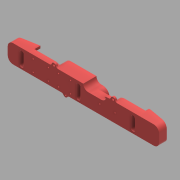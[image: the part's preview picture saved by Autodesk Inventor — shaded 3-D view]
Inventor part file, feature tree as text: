
AUTODESK INVENTOR PART (.ipt)
format: ipt  version: 2017 (Build 210142000, 142)  size: 804,864 bytes
history: native  units: mm
features: reference x26, sketch x14, extrude x13, projected_geometry x10, fillet x9, other x9, chamfer x3, hole x2
ambient origin geometry x8: Origin, YZ Plane, XZ Plane, XY Plane, X Axis, Y Axis, Z Axis, Center Point
bodies: Solid1 (feature_tree)
feature tree (86):
  extrude  "Extrusion1"  TaperAngle=0.0deg  [1 undecoded]
  extrude  "Extrusion4"  Depth=17.453293mm
  extrude  "Extrusion5"  Depth=4.6mm
  fillet  "Fillet1"  Radius=4.6mm
  hole  "Hole1"  [1 undecoded]
  extrude  "Extrusion8"  Depth=2.5mm
  extrude  "Extrusion9"  Depth=3.0mm
  extrude  "Extrusion10"  Depth=1.6mm
  fillet  "Fillet5"  Radius=1.6mm
  extrude  "Extrusion11"  Depth=2.0mm TaperAngle=0.0deg
  fillet  "Fillet6"  Radius=10.0mm
  extrude  "Extrusion12"  Depth=4.0mm
  extrude  "Extrusion13"  Depth=1.2mm
  fillet  "Fillet7"  Radius=1.2mm
  fillet  "Fillet8"  Radius=3.0mm
  fillet  "Fillet9"  Radius=3.0mm
  fillet  "Fillet10"  Radius=3.0mm
  extrude  "Extrusion14"  Depth=2.0mm
  fillet  "Fillet11"  Radius=2.0mm
  sketch  "Sketch17"  dims[d76=1.75mm d77=25.0mm d78=2.0mm]
  extrude  "Extrusion15"  Depth=3.0mm TaperAngle=0.0deg
  fillet  "Fillet12"  Radius=4.75mm
  hole  "Hole4"  [1 undecoded]
  extrude  "Extrusion16"  Depth=2.0mm
  chamfer  "Chamfer1"  Distance=16.0mm
  extrude  "Extrusion17"  Depth=2.0mm
  chamfer  "Chamfer2"  Distance=3.5mm
  chamfer  "Chamfer3"  Distance=4.6mm
  sketch  "Sketch1"  dims[d0=17.453293mm d1=0.0mm]
  reference  "Reference1"
  reference  "Reference2"
  reference  "Reference3"
  reference  "Reference4"
  reference  "Reference5"
  reference  "Reference6"
  sketch  "Sketch4"  dims[d2=0.0mm d3=17.453293mm]
  projected_geometry  "Projected Loop3"
  reference  "Reference7"
  reference  "Reference8"
  reference  "Reference9"
  reference  "Reference10"
  reference  "Reference11"
  reference  "Reference12"
  reference  "Reference13"
  sketch  "Sketch5"  dims[d4=20.0mm d5=0.0mm d6=8.0mm d16=4.6mm]
  projected_geometry  "Projected Loop4"
  projected_geometry  "Projected Loop5"
  reference  "Reference18"
  reference  "Reference19"
  reference  "Reference20"
  reference  "Reference21"
  reference  "Reference22"
  reference  "Reference23"
  reference  "Reference24"
  reference  "Reference25"
  sketch  "Sketch9"  dims[d17=1.5mm d18=0.0mm d19=4.6mm]
  sketch  "Sketch10"  dims[d20=4.6mm d21=2.5mm]
  reference  "Reference29"
  sketch  "Sketch11"  dims[d22=1.5mm d23=0.0mm d24=3.0mm]
  projected_geometry  "Projected Loop7"
  projected_geometry  "Projected Loop12"
  projected_geometry  "Projected Loop13"
  sketch  "Sketch13"  dims[d32=1.4mm d33=6.0mm d34=4.0mm d35=2.0mm d36=90.0deg d37=8.0mm d38=20.594885mm d48=1.6mm d49=1.6mm]
  projected_geometry  "Projected Loop14"
  sketch  "Sketch14"  dims[d50=2.0mm d51=0.0mm d52=2.0mm d53=0.0mm d54=10.0mm]
  projected_geometry  "Projected Loop15"
  sketch  "Sketch15"  dims[d55=4.0mm d56=0.0mm d67=16.5mm]
  projected_geometry  "Projected Loop16"
  projected_geometry  "Projected Loop17"
  sketch  "Sketch16"  dims[d69=3.5mm d70=1.2mm d71=1.2mm d72=3.0mm d73=3.0mm d74=3.0mm d75=0.0mm]
  sketch  "Sketch18"  dims[d79=3.0mm d80=0.0mm d81=3.0mm d82=0.0mm d83=4.75mm]
  sketch  "Sketch19"  dims[d84=5.75mm d85=7.25mm]
  reference  "Reference30"
  reference  "Reference31"
  sketch  "Sketch20"  dims[d86=5.0mm d87=158.0mm d88=16.0mm d89=64.0mm d90=3.5mm d91=4.6mm d92=4.6mm d93=2.0mm d94=0.0mm d95=51.5mm d96=21.5mm d97=4.6mm d98=2.5mm d99=4.6mm d100=2.0mm d101=0.0mm d102=4.6mm d103=4.6mm d104=7.0mm d105=2.2mm d106=6.0mm d107=4.0mm d108=2.0mm d109=90.0deg d110=8.0mm d111=20.594885mm d112=2.0mm d113=0.0mm d114=0.5mm d115=2.0mm d116=45.0deg d117=2.0mm d118=0.0mm d119=0.5mm d120=2.0mm d121=45.0deg d122=0.5mm d123=2.0mm d124=45.0deg]
  reference  "Reference32"
  reference  "Reference33"
  other  "<userpath>\Dropbox\Work\HeadSLAM\xtion_custom_assembly.iam"
  other  "xtion_custom_assembly.iam"
  other  "xtion_heatsink:1"
  other  "xtion_projector:1"
  other  "xtion_mainboard:1"
  other  "xtion_rgb_cam:1"
  other  "xtion_ir_cam:1"
  other  "<userpath>\Dropbox\Work\HeadSLAM\xtion_custom_assembly_v2.iam"
  other  "xtion_custom_assembly_v2.iam"
note: 3 required parameter values undecoded (feature->parameter linkage not recoverable at this tier; creation-order binding heuristic only, values carry confidence <= 0.55)
